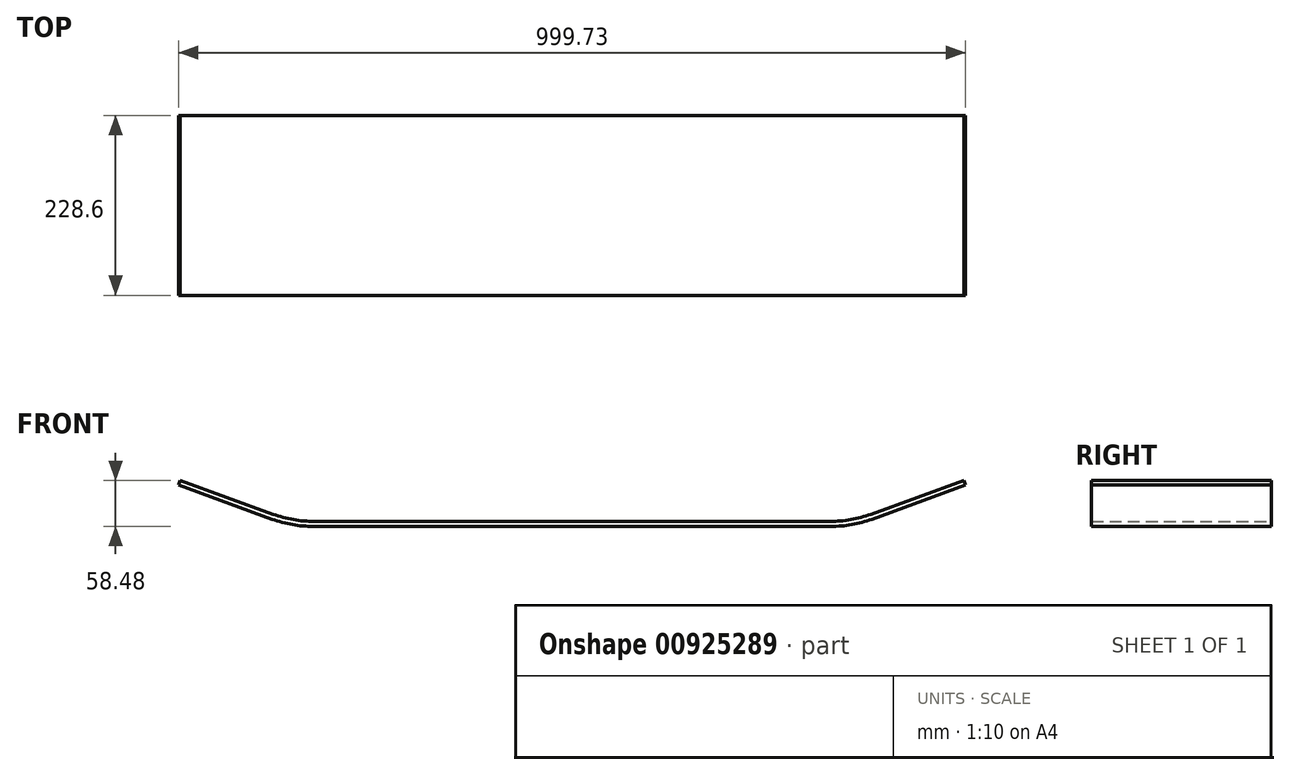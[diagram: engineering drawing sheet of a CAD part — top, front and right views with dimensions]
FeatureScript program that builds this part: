
annotation { "Feature Type Name" : "Feature", "Feature Type Description" : "" }
export const myFeature = defineFeature(function(context is Context, id is Id, definition is map)
    precondition{}
    {
        {
            var Q0;
            Q0=qCreatedBy(makeId("Front.planeOp"),FACE);
            var sketch = newSketch(context, id + "F0", { "sketchPlane" : qUnion([Q0])});
            skLineSegment(sketch, "E0.bottom", {"start": v(367.97, -16.58) * mm, "end": v(-289.48, -16.58) * mm});
            skLineSegment(sketch, "E0.top", {"start": v(366.85, -10.23) * mm, "end": v(-288.36, -10.23) * mm});
            skPoint(sketch, "E0.middle", {"position": v(0, 0) * mm});
            skLineSegment(sketch, "E1", {"start": v(-341.6, -7.39) * mm, "end": v(-460.62, 35.93) * mm});
            skLineSegment(sketch, "E2", {"start": v(-340.49, -1.04) * mm, "end": v(-458.45, 41.9) * mm});
            skLineSegment(sketch, "E3", {"start": v(-458.45, 41.9) * mm, "end": v(-460.62, 35.93) * mm});
            skLineSegment(sketch, "E4", {"start": v(418.98, -1.04) * mm, "end": v(536.93, 41.9) * mm});
            skLineSegment(sketch, "E5", {"start": v(539.1, 35.93) * mm, "end": v(420.1, -7.39) * mm});
            skLineSegment(sketch, "E6", {"start": v(536.93, 41.9) * mm, "end": v(539.1, 35.93) * mm});
            skPoint(sketch, "E7.visualSharp", {"position": v(-315.24, -10.23) * mm});
            skArc(sketch, "E7.filletArc", {"start": v(-340.49, -1.04) * mm, "mid": v(-314.83, -7.91) * mm, "end": v(-288.36, -10.23) * mm});
            skPoint(sketch, "E8.visualSharp", {"position": v(-316.36, -16.58) * mm});
            skArc(sketch, "E8.filletArc", {"start": v(-341.6, -7.39) * mm, "mid": v(-315.95, -14.26) * mm, "end": v(-289.48, -16.58) * mm});
            skPoint(sketch, "E9.visualSharp", {"position": v(394.84, -16.58) * mm});
            skArc(sketch, "E9.filletArc", {"start": v(367.97, -16.58) * mm, "mid": v(394.44, -14.26) * mm, "end": v(420.1, -7.39) * mm});
            skPoint(sketch, "E10.visualSharp", {"position": v(393.72, -10.23) * mm});
            skArc(sketch, "E10.filletArc", {"start": v(366.85, -10.23) * mm, "mid": v(393.32, -7.91) * mm, "end": v(418.98, -1.04) * mm});
            skSolve(sketch);
        }
        {
            var Q0;
            Q0 = qSketchRegion(id + "F0", true);
            extrude(context, id + "F1", {"entities" : qUnion([Q0]), "depth" : 228.6 * mm, "offsetDistance" : 25.4 * mm});
        }
    });
